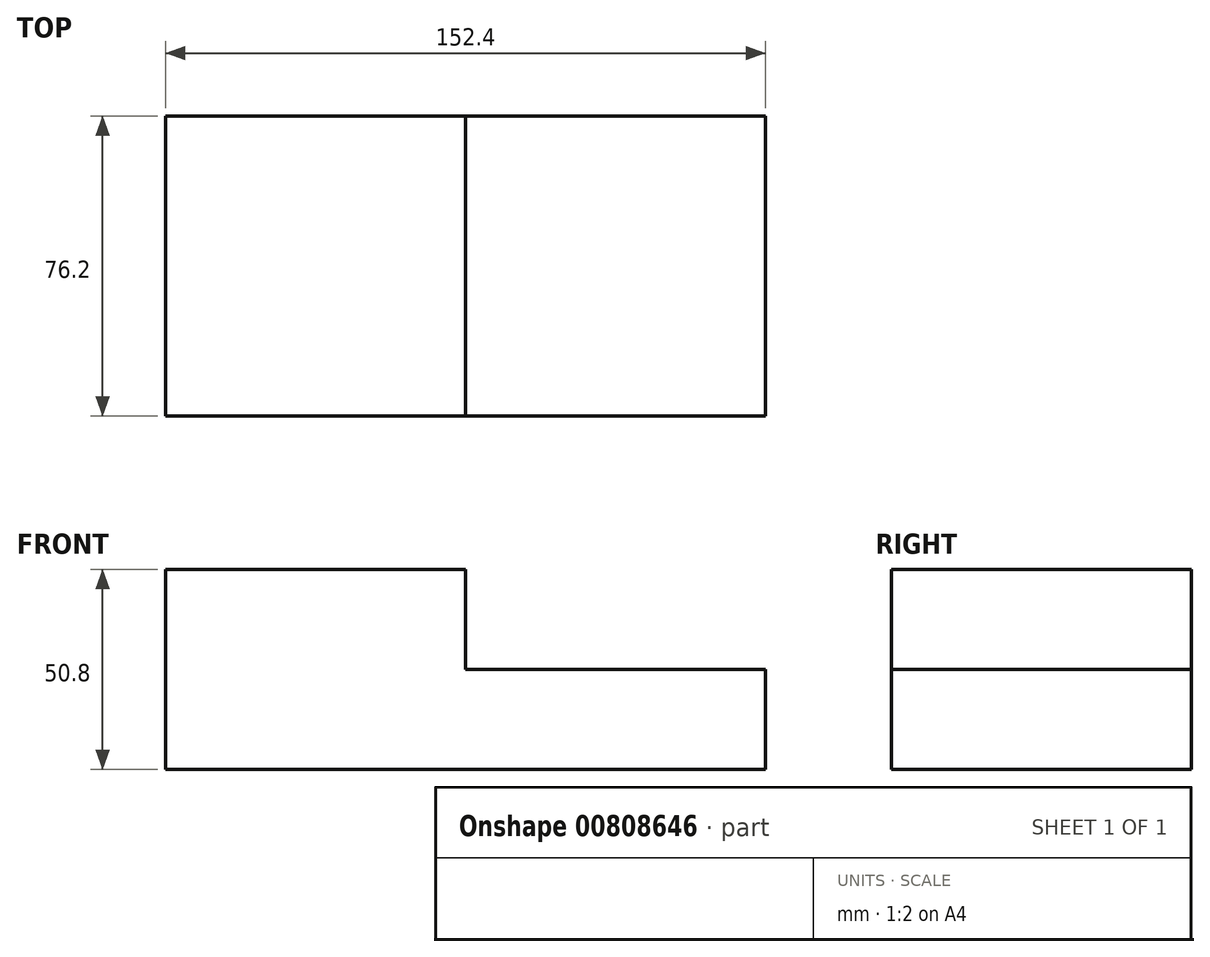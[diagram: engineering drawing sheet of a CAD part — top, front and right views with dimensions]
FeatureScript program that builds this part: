
annotation { "Feature Type Name" : "Feature", "Feature Type Description" : "" }
export const myFeature = defineFeature(function(context is Context, id is Id, definition is map)
    precondition{}
    {
        {
            var Q0;
            Q0=qCreatedBy(makeId("Front.planeOp"),FACE);
            var sketch = newSketch(context, id + "F0", { "sketchPlane" : qUnion([Q0])});
            skLineSegment(sketch, "E0.bottom", {"start": v(0, 0) * mm, "end": v(-76.2, 0) * mm});
            skLineSegment(sketch, "E0.top", {"start": v(0, 50.8) * mm, "end": v(-76.2, 50.8) * mm});
            skLineSegment(sketch, "E0.left", {"start": v(0, 0) * mm, "end": v(0, 50.8) * mm});
            skLineSegment(sketch, "E0.right", {"start": v(-76.2, 0) * mm, "end": v(-76.2, 50.8) * mm});
            skLineSegment(sketch, "E1.bottom", {"start": v(0, 0) * mm, "end": v(76.2, 0) * mm});
            skLineSegment(sketch, "E1.top", {"start": v(0, 25.4) * mm, "end": v(76.2, 25.4) * mm});
            skLineSegment(sketch, "E1.left", {"start": v(0, 0) * mm, "end": v(0, 25.4) * mm});
            skLineSegment(sketch, "E1.right", {"start": v(76.2, 0) * mm, "end": v(76.2, 25.4) * mm});
            skSolve(sketch);
        }
        {
            var Q0;
            Q0 = qSketchRegion(id + "F0", true);
            extrude(context, id + "F1", {"entities" : qUnion([Q0]), "depth" : 76.2 * mm, "offsetDistance" : 25.4 * mm});
        }
    });
